# Revit family: ALINE-58
name_source: partatom
category: Lighting Fixtures
units: mm (PartAtom-declared; Revit-internal decimal feet)

## family parameters
Always vertical = Yes
Cut with Voids When Loaded = No
Host = Ceiling
Light Source = Yes
OmniClass Number = 23.80.70.11
OmniClass Title = Luminaries for Internal Lighting
Part Type = Normal
Room Calculation Point = No
Round Connector Dimension = Use Diameter
Shared = No

## types (4) — shared parameters
AssetType = Movable
Brand = Pholc
Cable Length (default) = 700 mm  [stored 2.29659 ft]
Category = Pendants
Class = Class 2
Color = Aluminium /Frosted plastic
Color Filter = 16777215
Dimmable = Yes If the LS is Dimmable
Dimming Lamp Color Temperature Shift = <None>
IFC classification = Light Fixture
IP_Code = IP20
Light Source Symbol Size = 150 mm
LightFixtureMountingType = Pendants
LightFixturePlacingType = Ceiling
Lightsource included = No
Lightsource type = LED
Manufacturer = Pholc
Manufacturer Name = Pholc
ManufacturerName = Pholc
ManufacturerURL = https://www.pholc.se
Max watt = 25
Model Name = ALINE 58 pendant
ModelReference = ALINE 58 pendant
NBS Reference Description = General purpose luminaires
NBSReference = 90-60-50/405
Name = ALINE 58 pendant
Nominal Height = 192 mm  [stored 0.629921 ft]
Nominal Length = 580 mm  [stored 1.90289 ft]
Nominal Width = 580 mm  [stored 1.90289 ft]
NominalCurrent = 0 A
NominalVoltage = 0 V
Rechargeble = No
Shape = Cone
Size = 58 cm
Socket = E27
Surface Material = Frosted plastic
TotalWattage = 25 W
URL = https://www.pholc.se
https://www.pholc.se
Uniclass2015Description = Pendant luminaires
Uniclass2015Reference = Pr_70_70_48_62
VisualHusRef = Pholc_Id080

## per-type parameters (varying)
| type | ArticleNumber | Model | ModelNumber | Surface Material 2 |
| ALINE 58 pendant - 431114 | 431114 | 431114 | 431114 | Aluminum |
| ALINE 58 pendant - 431115 | 431115 | 431115 | 431115 | Black inc (NCS S 8500-N) |
| ALINE 58 pendant - 431118 | 431118 | 431118 | 431118 | Chamomile (NCS S 1020-G80Y) |
| ALINE 58 pendant - 431113 | 431113 | 431113 | 431113 | COTTON (NCS S 0502-Y) |

note: [stored X ft] marks values corroborated as IEEE doubles in the binary element streams (Revit-internal decimal feet)

## geometry (parser evidence)
native form markers: Sweep x1
no freeform markers — native parametric forms only
